# Revit family: Edge_TB42_H_Top_Hung_Standard
name_source: partatom
category: Windows
revit_build: Autodesk Revit 2014 (Build: 20130308_1515(x64)
units: mm (PartAtom-declared; Revit-internal decimal feet)

## types (12) — shared parameters
Aluminium Thickness = 1 mm  [stored 0.00328084 ft]
Bead SG Gap = 13 mm
Bottom Hung = No
Casement Dimension = 42 mm  [stored 0.137795 ft]
Custom Sash Bottom Height = 554 mm  [stored 1.81759 ft]
Custom Sash Top Height = 554 mm  [stored 1.81759 ft]
DG Extrusion Start = 11 mm  [stored 0.0360892 ft]
DG Gasket Finish = Double Glazing Gasket Material
DG Thickness Calc = 4 mm  [stored 0.0131234 ft]
Default Sill Height = 800 mm  [stored 2.62467 ft]
Depth Bead = 28 mm  [stored 0.0918635 ft]
Description = Thermal break casement windows (42mm), Type H top hung
Frame Center Offset = 21 mm  [stored 0.0688976 ft]
Height Panel 1 = 540 mm  [stored 1.77165 ft]
Height Panel 2 = 540 mm  [stored 1.77165 ft]
Height Sash 1 = 524 mm  [stored 1.71916 ft]
Height Sash 1 Opening = 554 mm  [stored 1.81759 ft]
Height Sash 2 = 524 mm  [stored 1.71916 ft]
Height Sash 2 Opening = 554 mm  [stored 1.81759 ft]
Limit Fixed Pane Height Max = 1800 mm
Limit Fixed Pane Height Min = 200 mm  [stored 0.656168 ft]
Limit Sash Height Max = 1200 mm
Limit Sash Height Min = 300 mm  [stored 0.984252 ft]
Limit Sash Width Max = 1500 mm
Limit Sash Width Min = 300 mm  [stored 0.984252 ft]
Limit Window Height Max = 3000 mm
Limit Window Height Min = 1400 mm
Limit Window Width Max = 1546 mm
Limit Window Width Min = 346 mm
Manufacturer = Crealco
Max System DG One Piece Thickness = 6 mm  [stored 0.019685 ft]
Max System DG Unit Thickness = 25 mm  [stored 0.082021 ft]
Model = Edge
Offset Bead SG Center Reversed = 21 mm  [stored 0.0688976 ft]
Offset Panel 3 Bead Top = 1170 mm
Offset Sash 1 Top = 23 mm  [stored 0.0754593 ft]
Offset Sash 2 Top = 593 mm  [stored 1.94554 ft]
Offset Sash Left = 23 mm  [stored 0.0754593 ft]
Offset Transom 1 Top = 570 mm  [stored 1.87008 ft]
Offset Transom 2 Top = 1140 mm  [stored 3.74016 ft]
Offset Window Exterior = 21 mm  [stored 0.0688976 ft]
SG Gasket Thickness = 6 mm  [stored 0.019685 ft]
Sash Center Offset = 18 mm
Sash Overlap = 7 mm  [stored 0.0229659 ft]
Sash Spacing Inner = 8 mm  [stored 0.0262467 ft]
Top Hung = Yes
URL = http://www.crealco.co.za
Wall Closure = By host
Width Bead = 15 mm  [stored 0.0492126 ft]
Width Profile = 30 mm  [stored 0.0984252 ft]
zero-valued in all types: Window Exterior Offset

## per-type parameters (varying)
- EDGE-0615DT-1000Pa: Area Pane Bottom=0.15 m²; Area Pane Middle=0.23 m²; Area Pane Top=0.23 m²; Clearvue Insulated LowE SHGC Value=0.389; Clearvue Insulated LowE U Value=2.82; Clearvue Insulated SHGC Value=0.427; Clearvue Insulated U Value=3.22; Clearvue SHGC Value=0.467; Clearvue U Value=5.14; Custom Windload=1000 mm  [stored 3.28084 ft]; Custom Window Height=1490 mm; Custom Window Width=590 mm  [stored 1.9357 ft]; Energy Advantage SHGC Value=0.419; Energy Advantage U Value=4.04; Height=1490 mm; Height Panel 3=290 mm; Intruderprufe Insulated LowE SHGC Value=0.354; Intruderprufe Insulated LowE U Value=2.78; Intruderprufe Insulated SHGC Value=0.391; Intruderprufe Insulated U Value=3.18; Intruderprufe LowE SHGC Value=0.393; Intruderprufe LowE U Value=4.04; Intruderprufe SHGC Value=0.435; Intruderprufe U Value=5.06; Length Transom=530 mm  [stored 1.73885 ft]; Max Pane Area=0.23 m²; Offset Mullion Left=559 mm; Offset Panel 4 Left=589 mm  [stored 1.93241 ft]; Sash Width=544 mm  [stored 1.78478 ft]; Width=590 mm  [stored 1.9357 ft]; Width Panel 1=530 mm  [stored 1.73885 ft]; Width Panel 2=530 mm  [stored 1.73885 ft]; Width Panel 3=530 mm  [stored 1.73885 ft]; Width Sash 1=514 mm; Width Sash 2=514 mm; Width Sash Opening=544 mm  [stored 1.78478 ft]; Windload Design=1000 mm  [stored 3.28084 ft]
- EDGE-0915DT-1000Pa: Area Pane Bottom=0.23 m²; Area Pane Middle=0.37 m²; Area Pane Top=0.37 m²; Clearvue Insulated LowE SHGC Value=0.431; Clearvue Insulated LowE U Value=2.7; Clearvue Insulated SHGC Value=0.474; Clearvue Insulated U Value=3.15; Clearvue SHGC Value=0.523; Clearvue U Value=5.25; Custom Windload=1000 mm  [stored 3.28084 ft]; Custom Window Height=1490 mm; Custom Window Width=890 mm  [stored 2.91995 ft]; Energy Advantage SHGC Value=0.469; Energy Advantage U Value=3.99; Height=1490 mm; Height Panel 3=290 mm; Intruderprufe Insulated LowE SHGC Value=0.392; Intruderprufe Insulated LowE U Value=2.66; Intruderprufe Insulated SHGC Value=0.434; Intruderprufe Insulated U Value=3.11; Intruderprufe LowE SHGC Value=0.439; Intruderprufe LowE U Value=3.99; Intruderprufe SHGC Value=0.487; Intruderprufe U Value=5.17; Length Transom=830 mm  [stored 2.7231 ft]; Max Pane Area=0.37 m²; Offset Mullion Left=859 mm  [stored 2.81824 ft]; Offset Panel 4 Left=889 mm  [stored 2.91667 ft]; Sash Width=844 mm  [stored 2.76903 ft]; Width=890 mm  [stored 2.91995 ft]; Width Panel 1=830 mm  [stored 2.7231 ft]; Width Panel 2=830 mm  [stored 2.7231 ft]; Width Panel 3=830 mm  [stored 2.7231 ft]; Width Sash 1=814 mm  [stored 2.6706 ft]; Width Sash 2=814 mm  [stored 2.6706 ft]; Width Sash Opening=844 mm  [stored 2.76903 ft]; Windload Design=1000 mm  [stored 3.28084 ft]
- EDGE-0618DT-1000Pa: Area Pane Bottom=0.3 m²; Area Pane Middle=0.23 m²; Area Pane Top=0.23 m²; Clearvue Insulated LowE SHGC Value=0.421; Clearvue Insulated LowE U Value=2.73; Clearvue Insulated SHGC Value=0.463; Clearvue Insulated U Value=3.17; Clearvue SHGC Value=0.508; Clearvue U Value=5.23; Custom Windload=1000 mm  [stored 3.28084 ft]; Custom Window Height=1790 mm; Custom Window Width=590 mm  [stored 1.9357 ft]; Energy Advantage SHGC Value=0.455; Energy Advantage U Value=4.01; Height=1790 mm; Height Panel 3=590 mm  [stored 1.9357 ft]; Intruderprufe Insulated LowE SHGC Value=0.384; Intruderprufe Insulated LowE U Value=2.69; Intruderprufe Insulated SHGC Value=0.424; Intruderprufe Insulated U Value=3.13; Intruderprufe LowE SHGC Value=0.426; Intruderprufe LowE U Value=4.01; Intruderprufe SHGC Value=0.473; Intruderprufe U Value=5.14; Length Transom=530 mm  [stored 1.73885 ft]; Max Pane Area=0.3 m²; Offset Mullion Left=559 mm; Offset Panel 4 Left=589 mm  [stored 1.93241 ft]; Sash Width=544 mm  [stored 1.78478 ft]; Width=590 mm  [stored 1.9357 ft]; Width Panel 1=530 mm  [stored 1.73885 ft]; Width Panel 2=530 mm  [stored 1.73885 ft]; Width Panel 3=530 mm  [stored 1.73885 ft]; Width Sash 1=514 mm; Width Sash 2=514 mm; Width Sash Opening=544 mm  [stored 1.78478 ft]; Windload Design=1000 mm  [stored 3.28084 ft]
- EDGE-0918DT-1000Pa: Area Pane Bottom=0.48 m²; Area Pane Middle=0.37 m²; Area Pane Top=0.37 m²; Clearvue Insulated LowE SHGC Value=0.462; Clearvue Insulated LowE U Value=2.61; Clearvue Insulated SHGC Value=0.507; Clearvue Insulated U Value=3.1; Clearvue SHGC Value=0.562; Clearvue U Value=5.33; Custom Windload=1000 mm  [stored 3.28084 ft]; Custom Window Height=1790 mm; Custom Window Width=890 mm  [stored 2.91995 ft]; Energy Advantage SHGC Value=0.503; Energy Advantage U Value=3.97; Height=1790 mm; Height Panel 3=590 mm  [stored 1.9357 ft]; Intruderprufe Insulated LowE SHGC Value=0.42; Intruderprufe Insulated LowE U Value=2.57; Intruderprufe Insulated SHGC Value=0.466; Intruderprufe Insulated U Value=3.06; Intruderprufe LowE SHGC Value=0.47; Intruderprufe LowE U Value=3.96; Intruderprufe SHGC Value=0.525; Intruderprufe U Value=5.24; Length Transom=830 mm  [stored 2.7231 ft]; Max Pane Area=0.48 m²; Offset Mullion Left=859 mm  [stored 2.81824 ft]; Offset Panel 4 Left=889 mm  [stored 2.91667 ft]; Sash Width=844 mm  [stored 2.76903 ft]; Width=890 mm  [stored 2.91995 ft]; Width Panel 1=830 mm  [stored 2.7231 ft]; Width Panel 2=830 mm  [stored 2.7231 ft]; Width Panel 3=830 mm  [stored 2.7231 ft]; Width Sash 1=814 mm  [stored 2.6706 ft]; Width Sash 2=814 mm  [stored 2.6706 ft]; Width Sash Opening=844 mm  [stored 2.76903 ft]; Windload Design=1000 mm  [stored 3.28084 ft]
- EDGE-0615DT-1500Pa: Area Pane Bottom=0.15 m²; Area Pane Middle=0.23 m²; Area Pane Top=0.23 m²; Clearvue Insulated LowE SHGC Value=0.389; Clearvue Insulated LowE U Value=2.82; Clearvue Insulated SHGC Value=0.427; Clearvue Insulated U Value=3.22; Clearvue SHGC Value=0.467; Clearvue U Value=5.14; Custom Windload=1500 mm; Custom Window Height=1490 mm; Custom Window Width=590 mm  [stored 1.9357 ft]; Energy Advantage SHGC Value=0.419; Energy Advantage U Value=4.04; Height=1490 mm; Height Panel 3=290 mm; Intruderprufe Insulated LowE SHGC Value=0.354; Intruderprufe Insulated LowE U Value=2.78; Intruderprufe Insulated SHGC Value=0.391; Intruderprufe Insulated U Value=3.18; Intruderprufe LowE SHGC Value=0.393; Intruderprufe LowE U Value=4.04; Intruderprufe SHGC Value=0.435; Intruderprufe U Value=5.06; Length Transom=530 mm  [stored 1.73885 ft]; Max Pane Area=0.23 m²; Offset Mullion Left=559 mm; Offset Panel 4 Left=589 mm  [stored 1.93241 ft]; Sash Width=544 mm  [stored 1.78478 ft]; Width=590 mm  [stored 1.9357 ft]; Width Panel 1=530 mm  [stored 1.73885 ft]; Width Panel 2=530 mm  [stored 1.73885 ft]; Width Panel 3=530 mm  [stored 1.73885 ft]; Width Sash 1=514 mm; Width Sash 2=514 mm; Width Sash Opening=544 mm  [stored 1.78478 ft]; Windload Design=1500 mm
- EDGE-0615DT-2000Pa: Area Pane Bottom=0.15 m²; Area Pane Middle=0.23 m²; Area Pane Top=0.23 m²; Clearvue Insulated LowE SHGC Value=0.389; Clearvue Insulated LowE U Value=2.82; Clearvue Insulated SHGC Value=0.427; Clearvue Insulated U Value=3.22; Clearvue SHGC Value=0.467; Clearvue U Value=5.14; Custom Windload=2000 mm; Custom Window Height=1490 mm; Custom Window Width=590 mm  [stored 1.9357 ft]; Energy Advantage SHGC Value=0.419; Energy Advantage U Value=4.04; Height=1490 mm; Height Panel 3=290 mm; Intruderprufe Insulated LowE SHGC Value=0.354; Intruderprufe Insulated LowE U Value=2.78; Intruderprufe Insulated SHGC Value=0.391; Intruderprufe Insulated U Value=3.18; Intruderprufe LowE SHGC Value=0.393; Intruderprufe LowE U Value=4.04; Intruderprufe SHGC Value=0.435; Intruderprufe U Value=5.06; Length Transom=530 mm  [stored 1.73885 ft]; Max Pane Area=0.23 m²; Offset Mullion Left=559 mm; Offset Panel 4 Left=589 mm  [stored 1.93241 ft]; Sash Width=544 mm  [stored 1.78478 ft]; Width=590 mm  [stored 1.9357 ft]; Width Panel 1=530 mm  [stored 1.73885 ft]; Width Panel 2=530 mm  [stored 1.73885 ft]; Width Panel 3=530 mm  [stored 1.73885 ft]; Width Sash 1=514 mm; Width Sash 2=514 mm; Width Sash Opening=544 mm  [stored 1.78478 ft]; Windload Design=2000 mm
- EDGE-0915DT-1500Pa: Area Pane Bottom=0.23 m²; Area Pane Middle=0.37 m²; Area Pane Top=0.37 m²; Clearvue Insulated LowE SHGC Value=0.431; Clearvue Insulated LowE U Value=2.7; Clearvue Insulated SHGC Value=0.474; Clearvue Insulated U Value=3.15; Clearvue SHGC Value=0.523; Clearvue U Value=5.25; Custom Windload=1500 mm; Custom Window Height=1490 mm; Custom Window Width=890 mm  [stored 2.91995 ft]; Energy Advantage SHGC Value=0.469; Energy Advantage U Value=3.99; Height=1490 mm; Height Panel 3=290 mm; Intruderprufe Insulated LowE SHGC Value=0.392; Intruderprufe Insulated LowE U Value=2.66; Intruderprufe Insulated SHGC Value=0.434; Intruderprufe Insulated U Value=3.11; Intruderprufe LowE SHGC Value=0.439; Intruderprufe LowE U Value=3.99; Intruderprufe SHGC Value=0.487; Intruderprufe U Value=5.17; Length Transom=830 mm  [stored 2.7231 ft]; Max Pane Area=0.37 m²; Offset Mullion Left=859 mm  [stored 2.81824 ft]; Offset Panel 4 Left=889 mm  [stored 2.91667 ft]; Sash Width=844 mm  [stored 2.76903 ft]; Width=890 mm  [stored 2.91995 ft]; Width Panel 1=830 mm  [stored 2.7231 ft]; Width Panel 2=830 mm  [stored 2.7231 ft]; Width Panel 3=830 mm  [stored 2.7231 ft]; Width Sash 1=814 mm  [stored 2.6706 ft]; Width Sash 2=814 mm  [stored 2.6706 ft]; Width Sash Opening=844 mm  [stored 2.76903 ft]; Windload Design=1500 mm
- EDGE-0915DT-2000Pa: Area Pane Bottom=0.23 m²; Area Pane Middle=0.37 m²; Area Pane Top=0.37 m²; Clearvue Insulated LowE SHGC Value=0.431; Clearvue Insulated LowE U Value=2.7; Clearvue Insulated SHGC Value=0.474; Clearvue Insulated U Value=3.15; Clearvue SHGC Value=0.523; Clearvue U Value=5.25; Custom Windload=2000 mm; Custom Window Height=1490 mm; Custom Window Width=890 mm  [stored 2.91995 ft]; Energy Advantage SHGC Value=0.469; Energy Advantage U Value=3.99; Height=1490 mm; Height Panel 3=290 mm; Intruderprufe Insulated LowE SHGC Value=0.392; Intruderprufe Insulated LowE U Value=2.66; Intruderprufe Insulated SHGC Value=0.434; Intruderprufe Insulated U Value=3.11; Intruderprufe LowE SHGC Value=0.439; Intruderprufe LowE U Value=3.99; Intruderprufe SHGC Value=0.487; Intruderprufe U Value=5.17; Length Transom=830 mm  [stored 2.7231 ft]; Max Pane Area=0.37 m²; Offset Mullion Left=859 mm  [stored 2.81824 ft]; Offset Panel 4 Left=889 mm  [stored 2.91667 ft]; Sash Width=844 mm  [stored 2.76903 ft]; Width=890 mm  [stored 2.91995 ft]; Width Panel 1=830 mm  [stored 2.7231 ft]; Width Panel 2=830 mm  [stored 2.7231 ft]; Width Panel 3=830 mm  [stored 2.7231 ft]; Width Sash 1=814 mm  [stored 2.6706 ft]; Width Sash 2=814 mm  [stored 2.6706 ft]; Width Sash Opening=844 mm  [stored 2.76903 ft]; Windload Design=2000 mm
- EDGE-0618DT-1500Pa: Area Pane Bottom=0.3 m²; Area Pane Middle=0.23 m²; Area Pane Top=0.23 m²; Clearvue Insulated LowE SHGC Value=0.421; Clearvue Insulated LowE U Value=2.73; Clearvue Insulated SHGC Value=0.463; Clearvue Insulated U Value=3.17; Clearvue SHGC Value=0.508; Clearvue U Value=5.23; Custom Windload=1500 mm; Custom Window Height=1790 mm; Custom Window Width=590 mm  [stored 1.9357 ft]; Energy Advantage SHGC Value=0.455; Energy Advantage U Value=4.01; Height=1790 mm; Height Panel 3=590 mm  [stored 1.9357 ft]; Intruderprufe Insulated LowE SHGC Value=0.384; Intruderprufe Insulated LowE U Value=2.69; Intruderprufe Insulated SHGC Value=0.424; Intruderprufe Insulated U Value=3.13; Intruderprufe LowE SHGC Value=0.426; Intruderprufe LowE U Value=4.01; Intruderprufe SHGC Value=0.473; Intruderprufe U Value=5.14; Length Transom=530 mm  [stored 1.73885 ft]; Max Pane Area=0.3 m²; Offset Mullion Left=559 mm; Offset Panel 4 Left=589 mm  [stored 1.93241 ft]; Sash Width=544 mm  [stored 1.78478 ft]; Width=590 mm  [stored 1.9357 ft]; Width Panel 1=530 mm  [stored 1.73885 ft]; Width Panel 2=530 mm  [stored 1.73885 ft]; Width Panel 3=530 mm  [stored 1.73885 ft]; Width Sash 1=514 mm; Width Sash 2=514 mm; Width Sash Opening=544 mm  [stored 1.78478 ft]; Windload Design=1500 mm
- EDGE-0618DT-2000Pa: Area Pane Bottom=0.3 m²; Area Pane Middle=0.23 m²; Area Pane Top=0.23 m²; Clearvue Insulated LowE SHGC Value=0.421; Clearvue Insulated LowE U Value=2.73; Clearvue Insulated SHGC Value=0.463; Clearvue Insulated U Value=3.17; Clearvue SHGC Value=0.508; Clearvue U Value=5.23; Custom Windload=2000 mm; Custom Window Height=1790 mm; Custom Window Width=590 mm  [stored 1.9357 ft]; Energy Advantage SHGC Value=0.455; Energy Advantage U Value=4.01; Height=1790 mm; Height Panel 3=590 mm  [stored 1.9357 ft]; Intruderprufe Insulated LowE SHGC Value=0.384; Intruderprufe Insulated LowE U Value=2.69; Intruderprufe Insulated SHGC Value=0.424; Intruderprufe Insulated U Value=3.13; Intruderprufe LowE SHGC Value=0.426; Intruderprufe LowE U Value=4.01; Intruderprufe SHGC Value=0.473; Intruderprufe U Value=5.14; Length Transom=530 mm  [stored 1.73885 ft]; Max Pane Area=0.3 m²; Offset Mullion Left=559 mm; Offset Panel 4 Left=589 mm  [stored 1.93241 ft]; Sash Width=544 mm  [stored 1.78478 ft]; Width=590 mm  [stored 1.9357 ft]; Width Panel 1=530 mm  [stored 1.73885 ft]; Width Panel 2=530 mm  [stored 1.73885 ft]; Width Panel 3=530 mm  [stored 1.73885 ft]; Width Sash 1=514 mm; Width Sash 2=514 mm; Width Sash Opening=544 mm  [stored 1.78478 ft]; Windload Design=2000 mm
- EDGE-0918DT-1500Pa: Area Pane Bottom=0.48 m²; Area Pane Middle=0.37 m²; Area Pane Top=0.37 m²; Clearvue Insulated LowE SHGC Value=0.462; Clearvue Insulated LowE U Value=2.61; Clearvue Insulated SHGC Value=0.507; Clearvue Insulated U Value=3.1; Clearvue SHGC Value=0.562; Clearvue U Value=5.33; Custom Windload=1500 mm; Custom Window Height=1790 mm; Custom Window Width=890 mm  [stored 2.91995 ft]; Energy Advantage SHGC Value=0.503; Energy Advantage U Value=3.97; Height=1790 mm; Height Panel 3=590 mm  [stored 1.9357 ft]; Intruderprufe Insulated LowE SHGC Value=0.42; Intruderprufe Insulated LowE U Value=2.57; Intruderprufe Insulated SHGC Value=0.466; Intruderprufe Insulated U Value=3.06; Intruderprufe LowE SHGC Value=0.47; Intruderprufe LowE U Value=3.96; Intruderprufe SHGC Value=0.525; Intruderprufe U Value=5.24; Length Transom=830 mm  [stored 2.7231 ft]; Max Pane Area=0.48 m²; Offset Mullion Left=859 mm  [stored 2.81824 ft]; Offset Panel 4 Left=889 mm  [stored 2.91667 ft]; Sash Width=844 mm  [stored 2.76903 ft]; Width=890 mm  [stored 2.91995 ft]; Width Panel 1=830 mm  [stored 2.7231 ft]; Width Panel 2=830 mm  [stored 2.7231 ft]; Width Panel 3=830 mm  [stored 2.7231 ft]; Width Sash 1=814 mm  [stored 2.6706 ft]; Width Sash 2=814 mm  [stored 2.6706 ft]; Width Sash Opening=844 mm  [stored 2.76903 ft]; Windload Design=1500 mm
- EDGE-0918DT-2000Pa: Area Pane Bottom=0.48 m²; Area Pane Middle=0.37 m²; Area Pane Top=0.37 m²; Clearvue Insulated LowE SHGC Value=0.462; Clearvue Insulated LowE U Value=2.61; Clearvue Insulated SHGC Value=0.507; Clearvue Insulated U Value=3.1; Clearvue SHGC Value=0.562; Clearvue U Value=5.33; Custom Windload=2000 mm; Custom Window Height=1790 mm; Custom Window Width=890 mm  [stored 2.91995 ft]; Energy Advantage SHGC Value=0.503; Energy Advantage U Value=3.97; Height=1790 mm; Height Panel 3=590 mm  [stored 1.9357 ft]; Intruderprufe Insulated LowE SHGC Value=0.42; Intruderprufe Insulated LowE U Value=2.57; Intruderprufe Insulated SHGC Value=0.466; Intruderprufe Insulated U Value=3.06; Intruderprufe LowE SHGC Value=0.47; Intruderprufe LowE U Value=3.96; Intruderprufe SHGC Value=0.525; Intruderprufe U Value=5.24; Length Transom=830 mm  [stored 2.7231 ft]; Max Pane Area=0.48 m²; Offset Mullion Left=859 mm  [stored 2.81824 ft]; Offset Panel 4 Left=889 mm  [stored 2.91667 ft]; Sash Width=844 mm  [stored 2.76903 ft]; Width=890 mm  [stored 2.91995 ft]; Width Panel 1=830 mm  [stored 2.7231 ft]; Width Panel 2=830 mm  [stored 2.7231 ft]; Width Panel 3=830 mm  [stored 2.7231 ft]; Width Sash 1=814 mm  [stored 2.6706 ft]; Width Sash 2=814 mm  [stored 2.6706 ft]; Width Sash Opening=844 mm  [stored 2.76903 ft]; Windload Design=2000 mm

note: [stored X ft] marks values corroborated as IEEE doubles in the binary element streams (Revit-internal decimal feet)

## geometry (parser evidence)
native form markers: Blend x4, Extrusion x1, Sweep x21
no freeform markers — native parametric forms only
